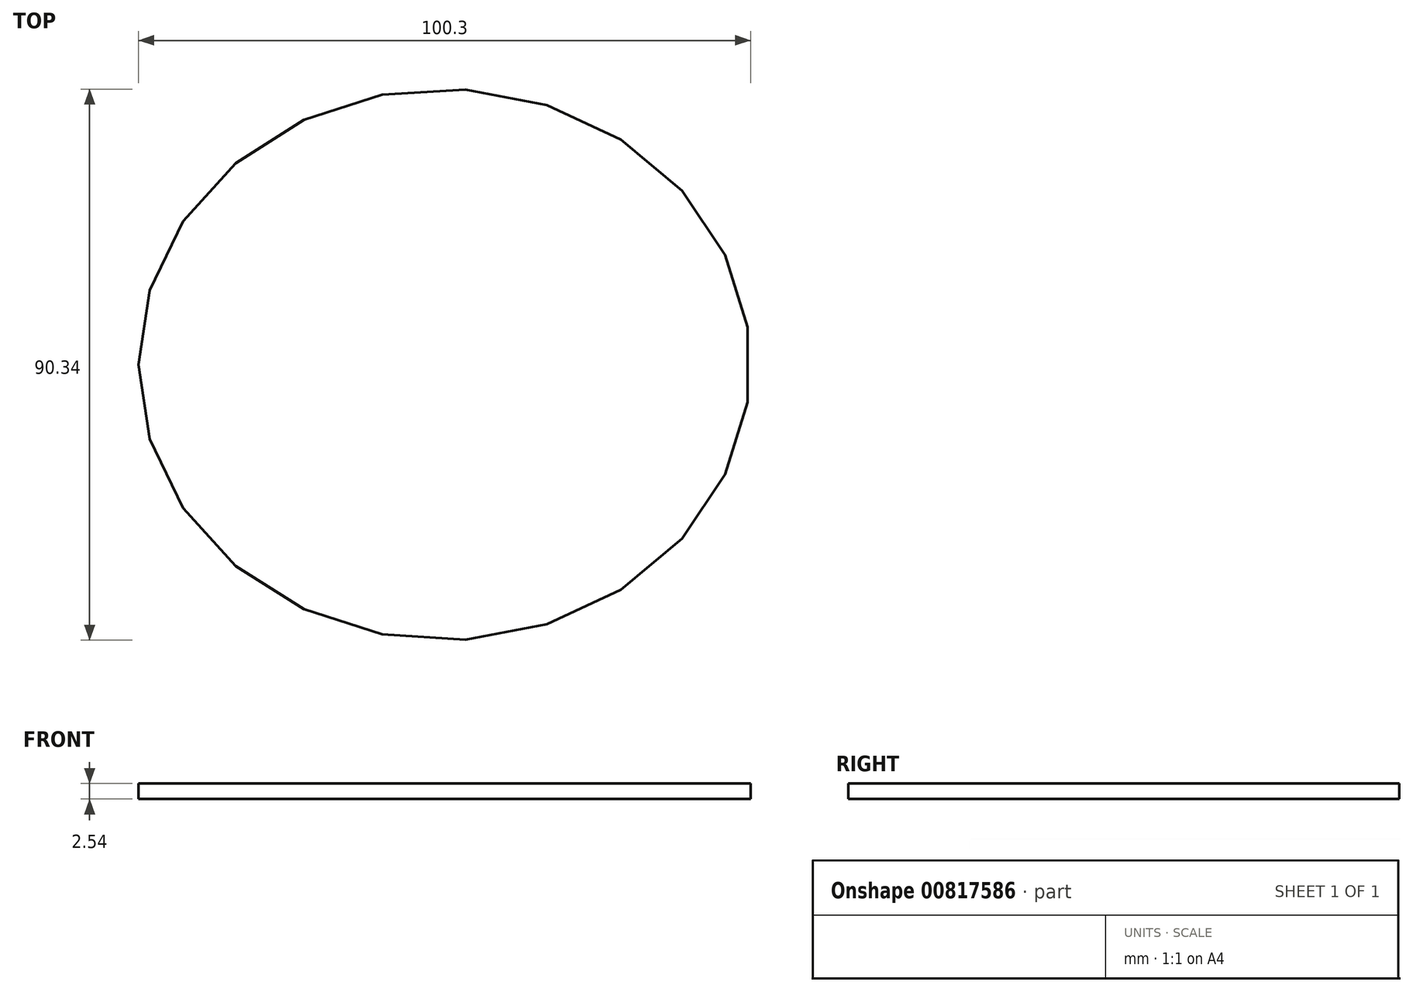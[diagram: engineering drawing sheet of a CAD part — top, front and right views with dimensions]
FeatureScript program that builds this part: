
annotation { "Feature Type Name" : "Feature", "Feature Type Description" : "" }
export const myFeature = defineFeature(function(context is Context, id is Id, definition is map)
    precondition{}
    {
        {
            var Q0;
            Q0=qCreatedBy(makeId("Top.planeOp"),FACE);
            var sketch = newSketch(context, id + "F0", { "sketchPlane" : qUnion([Q0])});
            skEllipse(sketch, "E0", {"center": v(0, -45.17) * mm, "majorRadius": 45.17 * mm, "minorRadius": 50.15 * mm, "majorAxis": v(0, 1)});
            skSolve(sketch);
        }
        {
            var Q0;
            Q0=makeQuery(id+"F0.imprint","IMPRINT",FACE,{"disambiguationData":[TD([[makeQuery(id+"F0.imprint","IMPRINT",EDGE,{"derivedFrom":sQuery(id+"F0.wireOp",EDGE,"E0")}),1.0]])]});
            extrude(context, id + "F1", {"entities" : qUnion([Q0]), "depth" : 2.54 * mm, "offsetDistance" : 25.4 * mm});
        }
    });
